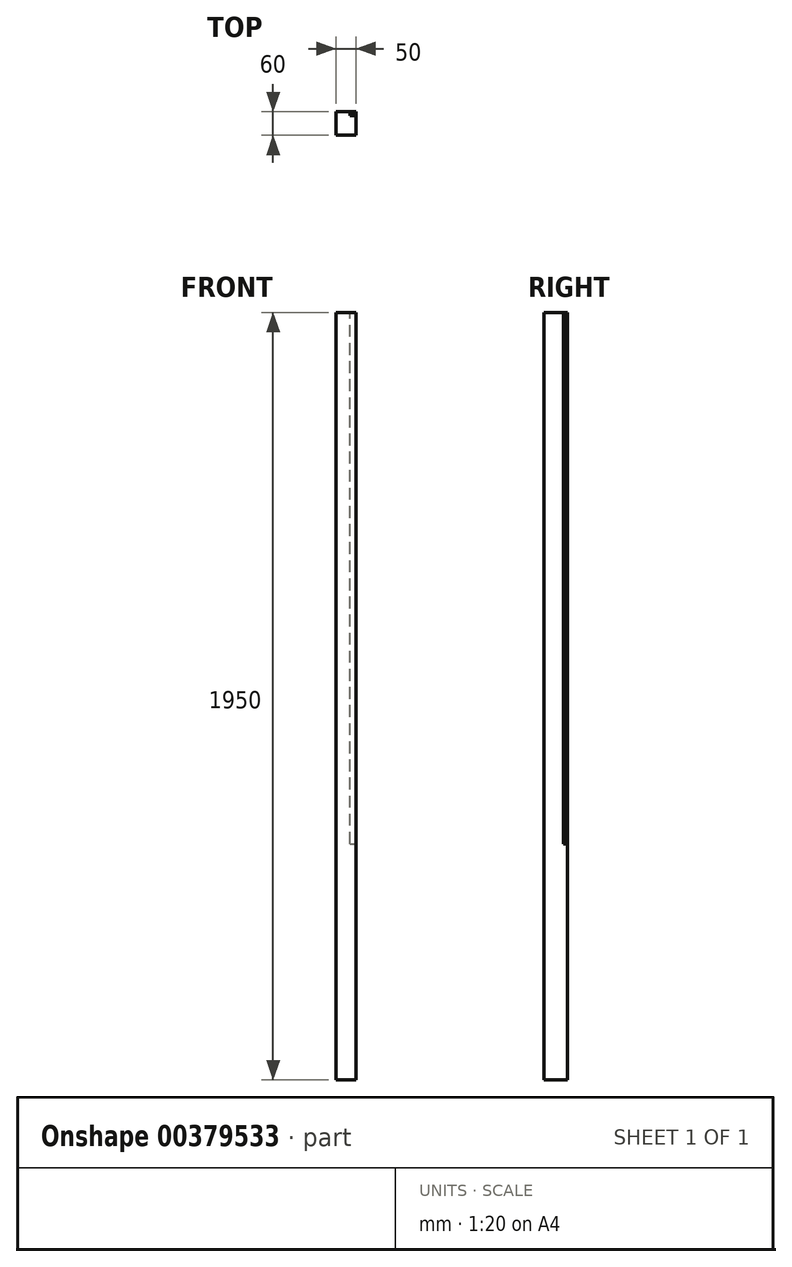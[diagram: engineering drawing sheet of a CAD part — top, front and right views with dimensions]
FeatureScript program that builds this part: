
annotation { "Feature Type Name" : "Feature", "Feature Type Description" : "" }
export const myFeature = defineFeature(function(context is Context, id is Id, definition is map)
    precondition{}
    {
        {
            var Q0;
            Q0=qCreatedBy(makeId("Top.planeOp"),FACE);
            var sketch = newSketch(context, id + "F0", { "sketchPlane" : qUnion([Q0])});
            skLineSegment(sketch, "E0.bottom", {"start": v(-25, 30) * mm, "end": v(25, 30) * mm});
            skLineSegment(sketch, "E0.top", {"start": v(-25, -30) * mm, "end": v(25, -30) * mm});
            skLineSegment(sketch, "E0.left", {"start": v(-25, 30) * mm, "end": v(-25, -30) * mm});
            skLineSegment(sketch, "E0.right", {"start": v(25, 30) * mm, "end": v(25, -30) * mm});
            skPoint(sketch, "E0.middle", {"position": v(0, 0) * mm});
            skSolve(sketch);
        }
        {
            var Q0;
            Q0=makeQuery(id+"F0.imprint","IMPRINT",FACE,{"disambiguationData":[TD([[makeQuery(id+"F0.imprint","IMPRINT",EDGE,{"derivedFrom":sQuery(id+"F0.wireOp",EDGE,"E0.bottom")}),-1.0]])]});
            extrude(context, id + "F1", {"entities" : qUnion([Q0]), "depth" : (150 * 9 + 600) * mm});
        }
        {
            var Q0;
            Q0=makeQuery(id+"F1.opExtrude","CAP_FACE",FACE,{"disambiguationData":[OSD([sQuery(id+"F0.wireOp",EDGE,"E0.bottom"),sQuery(id+"F0.wireOp",EDGE,"E0.top"),sQuery(id+"F0.wireOp",EDGE,"E0.left"),sQuery(id+"F0.wireOp",EDGE,"E0.right")])],"isStart":false});
            var sketch = newSketch(context, id + "F2", { "sketchPlane" : qUnion([Q0])});
            skLineSegment(sketch, "E1", {"start": v(25, 30) * mm, "end": v(10, 30) * mm});
            skLineSegment(sketch, "E2", {"start": v(10, 30) * mm, "end": v(10, 28) * mm});
            skLineSegment(sketch, "E3", {"start": v(10, 28) * mm, "end": v(25, 28) * mm});
            skLineSegment(sketch, "E4", {"start": v(25, 28) * mm, "end": v(25, 26) * mm});
            skLineSegment(sketch, "E5", {"start": v(25, 26) * mm, "end": v(10, 26) * mm});
            skLineSegment(sketch, "E6", {"start": v(10, 26) * mm, "end": v(10, 24) * mm});
            skLineSegment(sketch, "E7", {"start": v(10, 24) * mm, "end": v(25, 24) * mm});
            skLineSegment(sketch, "E8", {"start": v(25, 24) * mm, "end": v(25, 22) * mm});
            skLineSegment(sketch, "E9", {"start": v(25, 22) * mm, "end": v(10, 22) * mm});
            skLineSegment(sketch, "E10", {"start": v(10, 22) * mm, "end": v(10, 20) * mm});
            skLineSegment(sketch, "E11", {"start": v(10, 20) * mm, "end": v(25, 20) * mm});
            skSolve(sketch);
        }
        {
            var Q0;
            {var subQ0=sQuery(id+"F2.wireOp",EDGE,"E1");Q0=makeQuery(id+"F2.imprint","IMPRINT",FACE,{"disambiguationData":[TD([[makeQuery(id+"F2.imprint","IMPRINT",EDGE,{"derivedFrom":subQ0}),-1.0]])]});}
            var Q1;
            {var subQ0=sQuery(id+"F2.wireOp",EDGE,"E5");Q1=makeQuery(id+"F2.imprint","IMPRINT",FACE,{"disambiguationData":[TD([[makeQuery(id+"F2.imprint","IMPRINT",EDGE,{"derivedFrom":subQ0}),1.0]])]});}
            var Q2;
            {var subQ0=sQuery(id+"F2.wireOp",EDGE,"E9");Q2=makeQuery(id+"F2.imprint","IMPRINT",FACE,{"disambiguationData":[TD([[makeQuery(id+"F2.imprint","IMPRINT",EDGE,{"derivedFrom":subQ0}),1.0]])]});}
            extrude(context, id + "F3", {"entities" : qUnion([Q0, Q1, Q2]), "operationType" : NewBodyOperationType.REMOVE, "oppositeDirection" : true, "depth" : (150 * 9) * mm});
        }
    });
